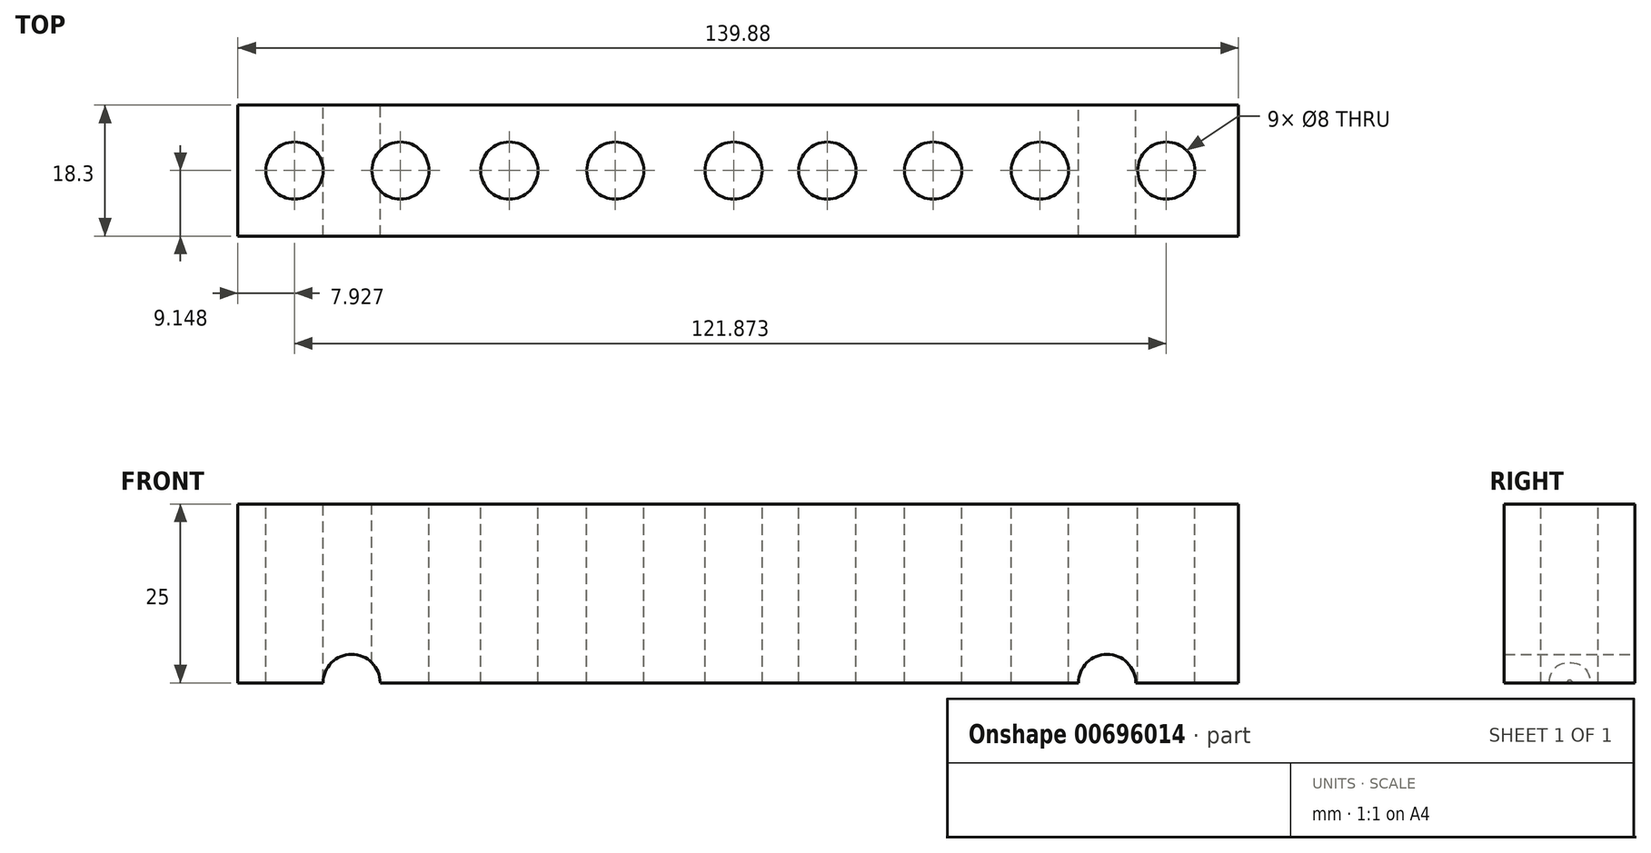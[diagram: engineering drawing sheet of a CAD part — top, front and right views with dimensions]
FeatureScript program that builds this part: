
annotation { "Feature Type Name" : "Feature", "Feature Type Description" : "" }
export const myFeature = defineFeature(function(context is Context, id is Id, definition is map)
    precondition{}
    {
        {
            var Q0;
            Q0=qCreatedBy(makeId("Top.planeOp"),FACE);
            var sketch = newSketch(context, id + "F0", { "sketchPlane" : qUnion([Q0])});
            skLineSegment(sketch, "E0.bottom", {"start": v(-69.3, 18.3) * mm, "end": v(70.58, 18.3) * mm});
            skLineSegment(sketch, "E0.top", {"start": v(-69.3, 0) * mm, "end": v(70.58, 0) * mm});
            skLineSegment(sketch, "E0.left", {"start": v(-69.3, 18.3) * mm, "end": v(-69.3, 0) * mm});
            skLineSegment(sketch, "E0.right", {"start": v(70.58, 18.3) * mm, "end": v(70.58, 0) * mm});
            skSolve(sketch);
        }
        {
            var Q0;
            Q0 = qSketchRegion(id + "F0", true);
            extrude(context, id + "F1", {"entities" : qUnion([Q0]), "depth" : 25 * mm, "offsetDistance" : 25 * mm});
        }
        {
            var Q0;
            Q0=makeQuery(id+"F1.opExtrude","CAP_FACE",FACE,{"disambiguationData":[OSD([sQuery(id+"F0.wireOp",EDGE,"E0.bottom"),sQuery(id+"F0.wireOp",EDGE,"E0.top"),sQuery(id+"F0.wireOp",EDGE,"E0.left"),sQuery(id+"F0.wireOp",EDGE,"E0.right")])],"isStart":false});
            var sketch = newSketch(context, id + "F2", { "sketchPlane" : qUnion([Q0])});
            skPoint(sketch, "E1", {"position": v(-61.37, 9.15) * mm});
            skPoint(sketch, "E1.positionSnap0", {"position": v(-69.3, 9.15) * mm});
            skPoint(sketch, "E2", {"position": v(-46.56, 9.15) * mm});
            skPoint(sketch, "E3", {"position": v(-31.34, 9.15) * mm});
            skPoint(sketch, "E4", {"position": v(-16.53, 9.15) * mm});
            skPoint(sketch, "E5", {"position": v(0, 9.15) * mm});
            skPoint(sketch, "E6", {"position": v(13.12, 9.15) * mm});
            skPoint(sketch, "E7", {"position": v(27.9, 9.15) * mm});
            skPoint(sketch, "E8", {"position": v(42.82, 9.15) * mm});
            skPoint(sketch, "E9", {"position": v(60.5, 9.15) * mm});
            skSolve(sketch);
        }
        {
            var Q0;
            Q0=sQuery(id+"F2.wireOp",VERTEX,"E1");
            var Q1;
            Q1=sQuery(id+"F2.wireOp",VERTEX,"E2");
            var Q2;
            Q2=sQuery(id+"F2.wireOp",VERTEX,"E3");
            var Q3;
            Q3=sQuery(id+"F2.wireOp",VERTEX,"E4");
            var Q4;
            Q4=sQuery(id+"F2.wireOp",VERTEX,"E5");
            var Q5;
            Q5=sQuery(id+"F2.wireOp",VERTEX,"E6");
            var Q6;
            Q6=sQuery(id+"F2.wireOp",VERTEX,"E7");
            var Q7;
            Q7=sQuery(id+"F2.wireOp",VERTEX,"E8");
            var Q8;
            Q8=sQuery(id+"F2.wireOp",VERTEX,"E9");
            var Q9;
            Q9=makeQuery(id+"F1.opExtrude","SWEPT_BODY",BODY,{"disambiguationData":[OSD([sQuery(id+"F0.wireOp",EDGE,"E0.bottom"),sQuery(id+"F0.wireOp",EDGE,"E0.top"),sQuery(id+"F0.wireOp",EDGE,"E0.left"),sQuery(id+"F0.wireOp",EDGE,"E0.right")])]});
            hole(context, id + "F3", {"style" : HoleStyle.SIMPLE, "endStyle" : HoleEndStyle.THROUGH, "holeDiameter" : 8 * mm, "majorDiameter" : 5 * mm, "isTappedThrough" : true, "tappedDepth" : 12 * mm, "tapClearance" : 3, "locations" : qUnion([Q0, Q1, Q2, Q3, Q4, Q5, Q6, Q7, Q8]), "scope" : qUnion([Q9])});
        }
        {
            var Q0;
            Q0=makeQuery(id+"F1.opExtrude","SWEPT_FACE",FACE,{"disambiguationData":[OSD([sQuery(id+"F0.wireOp",EDGE,"E0.bottom")])]});
            var sketch = newSketch(context, id + "F4", { "sketchPlane" : qUnion([Q0])});
            skPoint(sketch, "E10", {"position": v(-52.22, 0) * mm});
            skPoint(sketch, "E11", {"position": v(53.4, 0) * mm});
            skSolve(sketch);
        }
        {
            var Q0;
            Q0=sQuery(id+"F4.wireOp",VERTEX,"E10");
            var Q1;
            Q1=sQuery(id+"F4.wireOp",VERTEX,"E11");
            var Q2;
            Q2=makeQuery(id+"F1.opExtrude","SWEPT_BODY",BODY,{"disambiguationData":[OSD([sQuery(id+"F0.wireOp",EDGE,"E0.bottom"),sQuery(id+"F0.wireOp",EDGE,"E0.top"),sQuery(id+"F0.wireOp",EDGE,"E0.left"),sQuery(id+"F0.wireOp",EDGE,"E0.right")])]});
            hole(context, id + "F5", {"style" : HoleStyle.SIMPLE, "endStyle" : HoleEndStyle.THROUGH, "holeDiameter" : 8 * mm, "majorDiameter" : 5 * mm, "isTappedThrough" : true, "tappedDepth" : 12 * mm, "tapClearance" : 3, "locations" : qUnion([Q0, Q1]), "scope" : qUnion([Q2])});
        }
    });
